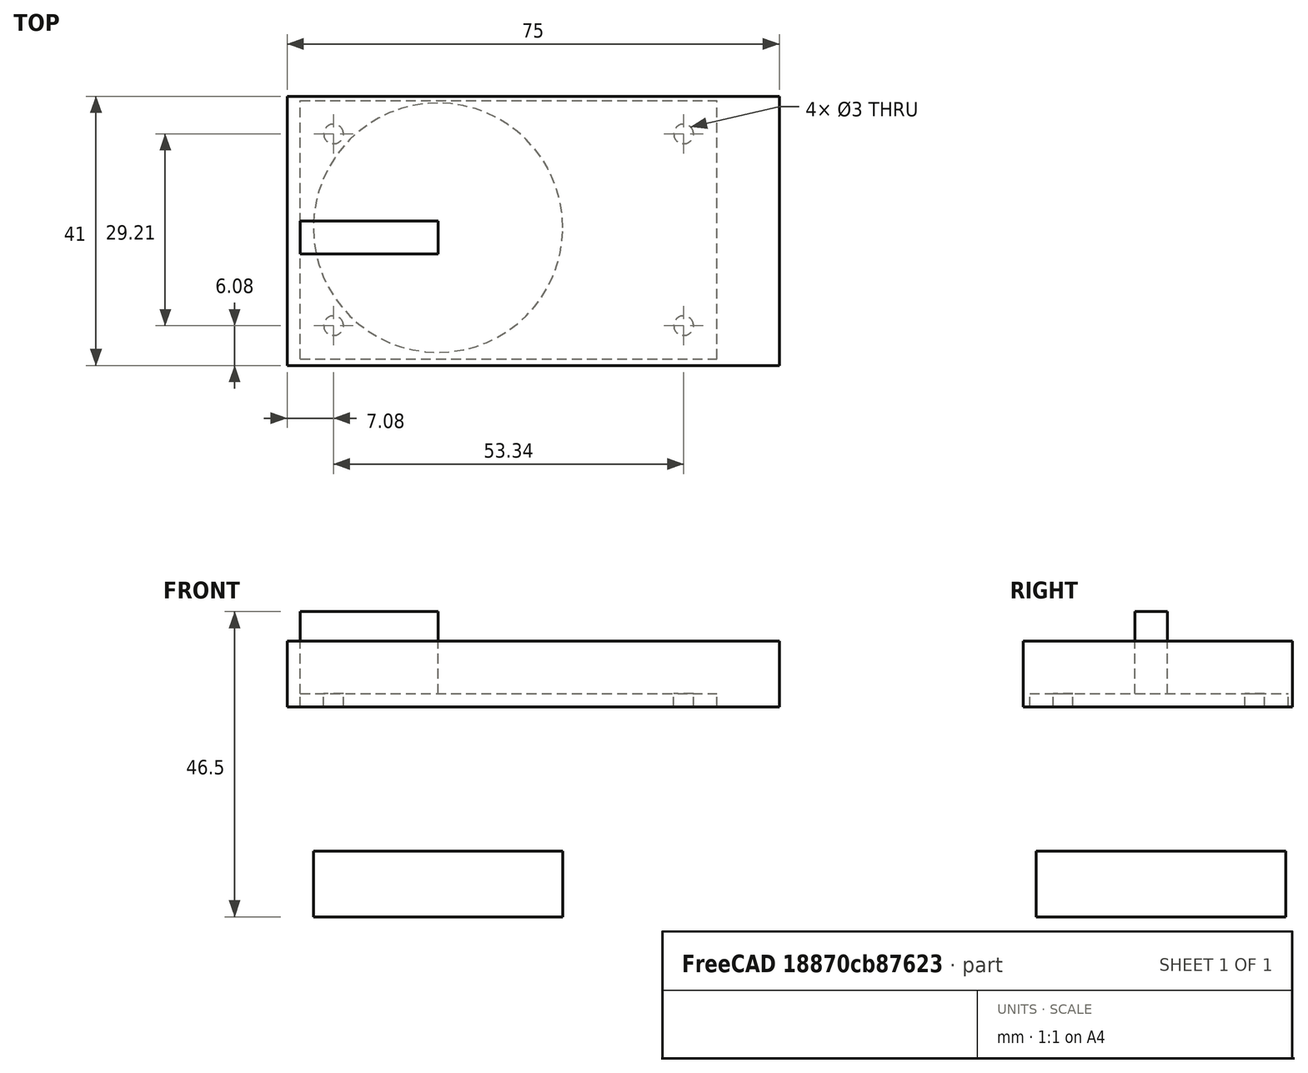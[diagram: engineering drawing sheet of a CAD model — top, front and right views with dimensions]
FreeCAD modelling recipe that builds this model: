
FCSTD DOCUMENT  (FreeCAD 0.14R3702 (Git))
Label: Plug Box
License: CC-BY 3.0
LicenseURL: http://creativecommons.org/licenses/by/3.0/
objects: Part::Cylinder×5, Part::Box×3, Part::Fuse×3, Part::Cut×1
note: 12 computed .brp shape members not serialized (recipe doc carries the construction recipe); baked Part::Feature solids carry a one-line shape summary decoded from their .brp

FEATURE [Part::Box] Box  label="Cube"
  Height = 2
  Length = 63.5
  Width = 39.37
FEATURE [Part::Box] Box001  label="Cube001"
  Height = 12.5
  Length = 21
  Placement = pos=(0,16,2) rot=(0,0,1;0rad)
  Width = 5
FEATURE [Part::Cylinder] Cylinder
  Angle = 360
  Height = 10
  Placement = pos=(5.08,5.08,-2) rot=(0,0,1;0rad)
  Radius = 1.5
FEATURE [Part::Cylinder] Cylinder001
  Angle = 360
  Height = 10
  Placement = pos=(5.08,34.29,-2) rot=(0,0,1;0rad)
  Radius = 1.5
FEATURE [Part::Cylinder] Cylinder002
  Angle = 360
  Height = 10
  Placement = pos=(58.42,5.08,-2) rot=(0,0,1;0rad)
  Radius = 1.5
FEATURE [Part::Cylinder] Cylinder003
  Angle = 360
  Height = 10
  Placement = pos=(58.42,34.29,-2) rot=(0,0,1;0rad)
  Radius = 1.5
FEATURE [Part::Fuse] Fusion
  Base = -> Cylinder
  Tool = -> Cylinder002
FEATURE [Part::Fuse] Fusion001
  Base = -> Cylinder001
  Tool = -> Cylinder003
FEATURE [Part::Fuse] Fusion002
  Base = -> Fusion
  Tool = -> Fusion001
FEATURE [Part::Cut] Cut
  Base = -> Box
  Tool = -> Fusion002
FEATURE [Part::Box] Box002  label="Cube002"
  Height = 10
  Length = 75
  Placement = pos=(-2,-1,0) rot=(0,0,1;0rad)
  Width = 41
FEATURE [Part::Cylinder] Cylinder004
  Angle = 360
  Height = 10
  Placement = pos=(21,20,-32) rot=(0,0,1;0rad)
  Radius = 19
